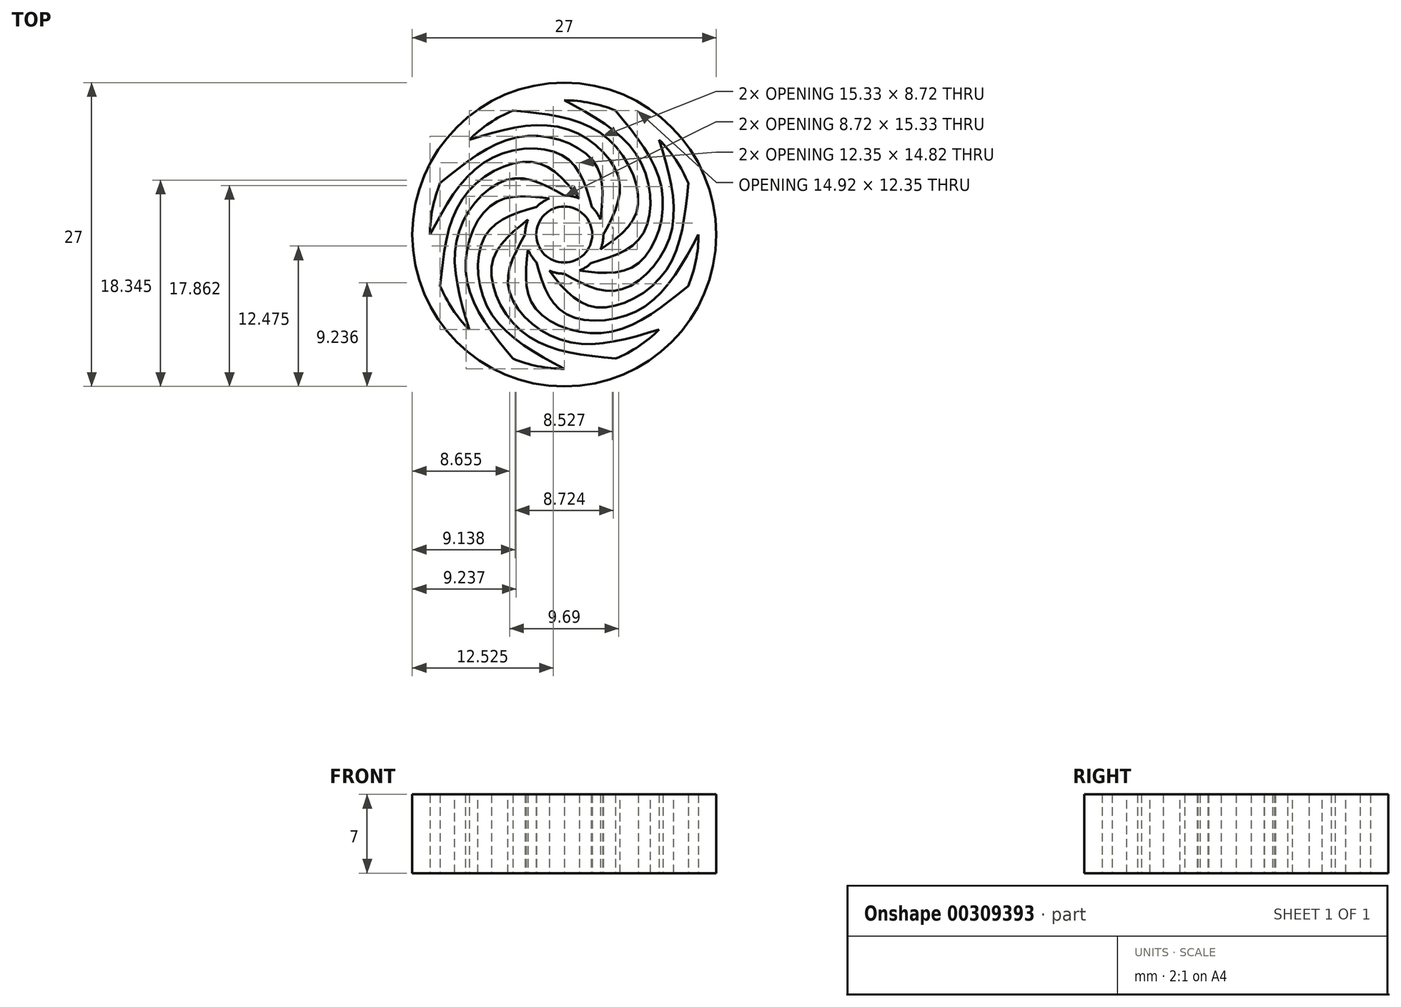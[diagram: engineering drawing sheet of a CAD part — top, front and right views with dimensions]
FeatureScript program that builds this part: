
annotation { "Feature Type Name" : "Feature", "Feature Type Description" : "" }
export const myFeature = defineFeature(function(context is Context, id is Id, definition is map)
    precondition{}
    {
        {
            var Q0;
            Q0=qCreatedBy(makeId("Top.planeOp"),FACE);
            var sketch = newSketch(context, id + "F0", { "sketchPlane" : qUnion([Q0])});
            skCircle(sketch, "E0", {"center": v(0, 0) * mm, "radius": 2.49 * mm});
            skCircle(sketch, "E1", {"center": v(0, 0) * mm, "radius": 3.48 * mm});
            skCircle(sketch, "E2", {"center": v(0, 0) * mm, "radius": 11.93 * mm});
            skFitSpline(sketch, "E3", {"points": [v(-11.02, 4.57) * mm, v(-3.61, 8.73) * mm, v(2.66, 6.42) * mm, v(3.21, 1.33) * mm], "startDerivative": vector(18.7, 15.37) * mm, "endDerivative": vector(-2.28, -19.06) * mm});
            skFitSpline(sketch, "E4", {"points": [v(-8.44, 8.44) * mm, v(0, 9.44) * mm, v(4.85, 4.98) * mm, v(3.48, 0) * mm], "startDerivative": vector(23.2, 7) * mm, "endDerivative": vector(-9.1, -16.95) * mm});
            skFitSpline(sketch, "E5", {"points": [v(-4.57, 11.02) * mm, v(3.61, 8.73) * mm, v(6.52, 2.4) * mm, v(3.21, -1.33) * mm], "startDerivative": vector(24.04, -2.2) * mm, "endDerivative": vector(-15.71, -10.92) * mm});
            skFitSpline(sketch, "E6", {"points": [v(0, 11.93) * mm, v(6.68, 6.68) * mm, v(6.95, 0) * mm, v(2.4, -2.52) * mm], "startDerivative": vector(21.35, -11.4) * mm, "endDerivative": vector(-18.29, -5.43) * mm});
            skFitSpline(sketch, "E7", {"points": [v(4.57, 11.02) * mm, v(8.73, 3.61) * mm, v(6.42, -2.66) * mm, v(1.33, -3.21) * mm], "startDerivative": vector(15.37, -18.7) * mm, "endDerivative": vector(-19.06, 2.28) * mm});
            skFitSpline(sketch, "E8", {"points": [v(8.44, 8.44) * mm, v(9.44, 0) * mm, v(4.92, -4.92) * mm, v(0, -3.48) * mm], "startDerivative": vector(7.04, -23.16) * mm, "endDerivative": vector(-16.74, 9.4) * mm});
            skFitSpline(sketch, "E9", {"points": [v(11.02, 4.57) * mm, v(8.73, -3.61) * mm, v(2.66, -6.42) * mm, v(-1.33, -3.21) * mm], "startDerivative": vector(-2.32, -24.08) * mm, "endDerivative": vector(-11.66, 15.2) * mm});
            skFitSpline(sketch, "E10", {"points": [v(11.93, 0) * mm, v(6.68, -6.68) * mm, v(0, -6.95) * mm, v(-2.46, -2.46) * mm], "startDerivative": vector(-11.4, -21.36) * mm, "endDerivative": vector(-5.2, 18.45) * mm});
            skFitSpline(sketch, "E11", {"points": [v(11.02, -4.57) * mm, v(3.61, -8.73) * mm, v(-2.66, -6.42) * mm, v(-3.21, -1.33) * mm], "startDerivative": vector(-18.7, -15.37) * mm, "endDerivative": vector(2.26, 19.04) * mm});
            skFitSpline(sketch, "E12", {"points": [v(8.44, -8.44) * mm, v(-0.02, -9.44) * mm, v(-4.92, -4.92) * mm, v(-3.48, 0) * mm], "startDerivative": vector(-23.2, -7.05) * mm, "endDerivative": vector(9.37, 16.72) * mm});
            skFitSpline(sketch, "E13", {"points": [v(4.57, -11.02) * mm, v(-3.61, -8.73) * mm, v(-6.42, -2.66) * mm, v(-3.21, 1.33) * mm], "startDerivative": vector(-24.1, 2.36) * mm, "endDerivative": vector(15.06, 11.86) * mm});
            skFitSpline(sketch, "E14", {"points": [v(0, -11.93) * mm, v(-6.72, -6.64) * mm, v(-6.95, 0) * mm, v(-2.46, 2.46) * mm], "startDerivative": vector(-21.46, 11.5) * mm, "endDerivative": vector(18.43, 5.21) * mm});
            skFitSpline(sketch, "E15", {"points": [v(-4.57, -11.02) * mm, v(-8.73, -3.61) * mm, v(-6.42, 2.66) * mm, v(-1.33, 3.21) * mm], "startDerivative": vector(-15.37, 18.7) * mm, "endDerivative": vector(19.04, -2.26) * mm});
            skFitSpline(sketch, "E16", {"points": [v(-8.44, -8.44) * mm, v(-9.44, 0) * mm, v(-4.92, 4.92) * mm, v(0, 3.48) * mm], "startDerivative": vector(-7.04, 23.16) * mm, "endDerivative": vector(16.72, -9.38) * mm});
            skFitSpline(sketch, "E17", {"points": [v(-11.02, -4.57) * mm, v(-8.73, 3.61) * mm, v(-2.66, 6.42) * mm, v(1.33, 3.21) * mm], "startDerivative": vector(2.36, 24.1) * mm, "endDerivative": vector(11.86, -15.06) * mm});
            skFitSpline(sketch, "E18", {"points": [v(-11.93, 0) * mm, v(-6.68, 6.68) * mm, v(0, 6.95) * mm, v(2.46, 2.46) * mm], "startDerivative": vector(11.4, 21.36) * mm, "endDerivative": vector(5.2, -18.45) * mm});
            skCircle(sketch, "E19", {"center": v(0, 0) * mm, "radius": 13.5 * mm});
            skSolve(sketch);
        }
        {
            var Q0;
            Q0=makeQuery(id+"F0.imprint","IMPRINT",FACE,{"disambiguationData":[TD([[makeQuery(id+"F0.imprint","IMPRINT",EDGE,{"derivedFrom":sQuery(id+"F0.wireOp",EDGE,"E19")}),1.0]])]});
            var Q1;
            {var subQ0=sQuery(id+"F0.wireOp",EDGE,"E9");Q1=makeQuery(id+"F0.imprint","IMPRINT",FACE,{"disambiguationData":[TD([[makeQuery(id+"F0.imprint","IMPRINT",EDGE,{"derivedFrom":subQ0}),1.0]])]});}
            var Q2;
            {var subQ0=sQuery(id+"F0.wireOp",EDGE,"E7");Q2=makeQuery(id+"F0.imprint","IMPRINT",FACE,{"disambiguationData":[TD([[makeQuery(id+"F0.imprint","IMPRINT",EDGE,{"derivedFrom":subQ0}),1.0]])]});}
            var Q3;
            {var subQ0=sQuery(id+"F0.wireOp",EDGE,"E5");Q3=makeQuery(id+"F0.imprint","IMPRINT",FACE,{"disambiguationData":[TD([[makeQuery(id+"F0.imprint","IMPRINT",EDGE,{"derivedFrom":subQ0}),1.0]])]});}
            var Q4;
            {var subQ0=sQuery(id+"F0.wireOp",EDGE,"E3");Q4=makeQuery(id+"F0.imprint","IMPRINT",FACE,{"disambiguationData":[TD([[makeQuery(id+"F0.imprint","IMPRINT",EDGE,{"derivedFrom":subQ0}),1.0]])]});}
            var Q5;
            {var subQ0=sQuery(id+"F0.wireOp",EDGE,"E17");Q5=makeQuery(id+"F0.imprint","IMPRINT",FACE,{"disambiguationData":[TD([[makeQuery(id+"F0.imprint","IMPRINT",EDGE,{"derivedFrom":subQ0}),1.0]])]});}
            var Q6;
            {var subQ0=sQuery(id+"F0.wireOp",EDGE,"E15");Q6=makeQuery(id+"F0.imprint","IMPRINT",FACE,{"disambiguationData":[TD([[makeQuery(id+"F0.imprint","IMPRINT",EDGE,{"derivedFrom":subQ0}),1.0]])]});}
            var Q7;
            {var subQ0=sQuery(id+"F0.wireOp",EDGE,"E13");Q7=makeQuery(id+"F0.imprint","IMPRINT",FACE,{"disambiguationData":[TD([[makeQuery(id+"F0.imprint","IMPRINT",EDGE,{"derivedFrom":subQ0}),1.0]])]});}
            var Q8;
            {var subQ0=sQuery(id+"F0.wireOp",EDGE,"E11");Q8=makeQuery(id+"F0.imprint","IMPRINT",FACE,{"disambiguationData":[TD([[makeQuery(id+"F0.imprint","IMPRINT",EDGE,{"derivedFrom":subQ0}),1.0]])]});}
            var Q9;
            Q9=makeQuery(id+"F0.imprint","IMPRINT",FACE,{"disambiguationData":[TD([[makeQuery(id+"F0.imprint","IMPRINT",EDGE,{"derivedFrom":sQuery(id+"F0.wireOp",EDGE,"E0")}),-1.0]])]});
            extrude(context, id + "F1", {"entities" : qUnion([Q0, Q1, Q2, Q3, Q4, Q5, Q6, Q7, Q8, Q9]), "depth" : 7 * mm});
        }
    });
